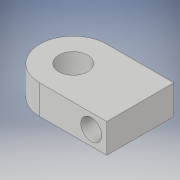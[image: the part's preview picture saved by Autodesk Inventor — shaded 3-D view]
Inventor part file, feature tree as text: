
AUTODESK INVENTOR PART (.ipt)
format: ipt  version: 2018 (Build 220112000, 112)  size: 134,656 bytes
history: native  units: in
note: dims shown in document units (in); Inventor stores cm internally (conversion verified against a paired STEP export)
features: sketch x7, extrude x6
ambient origin geometry x8: Origin, YZ Plane, XZ Plane, XY Plane, X Axis, Y Axis, Z Axis, Center Point
bodies: Solid1 (feature_tree)
feature tree (13):
  extrude  "Extrusion1"  Depth=0.8661in
  sketch  "Sketch2"  dims[d2=0.315in d3=0.4331in]
  sketch  "Sketch3"  dims[d4=0.378in d5=0.0in d6=0.2in]
  extrude  "Extrusion2"  Depth=0.4331in
  extrude  "Extrusion3"  Depth=0.378in
  extrude  "Extrusion4"  Depth=0.8661in
  extrude  "Extrusion5"  Depth=0.378in TaperAngle=0.0deg
  extrude  "Extrusion6"  Depth=0.378in
  sketch  "Sketch1"  dims[d0=0.6299in d1=0.8661in]
  sketch  "Sketch4"  dims[d8=0.2697in d10=0.8661in]
  sketch  "Sketch5"  dims[d11=0.378in d12=0.0in d13=0.378in d14=0.0in]
  sketch  "Sketch6"  dims[d15=0.378in d16=0.0in d17=0.5in]
  sketch  "Sketch7"  dims[d18=0.5in d19=0.0in d20=0.374in d21=0.3937in d22=0.0in]
